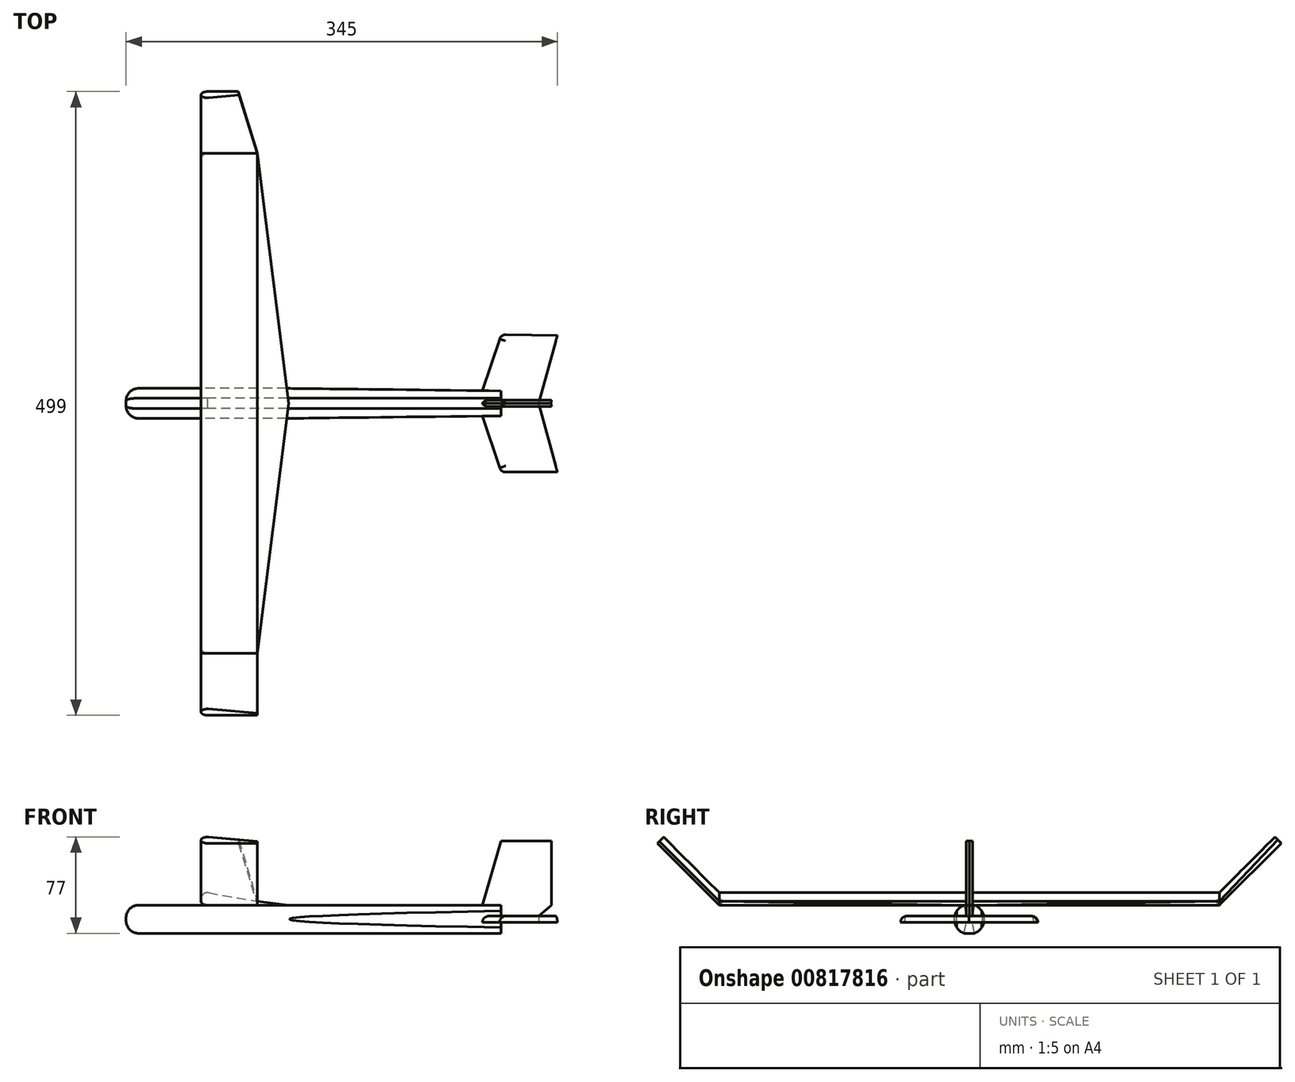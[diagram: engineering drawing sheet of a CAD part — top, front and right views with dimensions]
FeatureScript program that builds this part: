
annotation { "Feature Type Name" : "Feature", "Feature Type Description" : "" }
export const myFeature = defineFeature(function(context is Context, id is Id, definition is map)
    precondition{}
    {
        {
            var Q0;
            Q0=qCreatedBy(makeId("Top.planeOp"),FACE);
            var sketch = newSketch(context, id + "F0", { "sketchPlane" : qUnion([Q0])});
            skLineSegment(sketch, "E0", {"start": v(0, 0) * mm, "end": v(0, 200) * mm});
            skLineSegment(sketch, "E1", {"start": v(0, 0) * mm, "end": v(0, -200) * mm});
            skLineSegment(sketch, "E2", {"start": v(0, -200) * mm, "end": v(45, -200) * mm});
            skLineSegment(sketch, "E3", {"start": v(0, 200) * mm, "end": v(45, 200) * mm});
            skLineSegment(sketch, "E4", {"start": v(0, 0) * mm, "end": v(70, 0) * mm, "construction": true});
            skLineSegment(sketch, "E5", {"start": v(45, 200) * mm, "end": v(70, 0) * mm});
            skLineSegment(sketch, "E6", {"start": v(45, -200) * mm, "end": v(70, 0) * mm});
            skSolve(sketch);
        }
        {
            var Q0;
            Q0=makeQuery(id+"F0.imprint","IMPRINT",FACE,{"disambiguationData":[TD([[makeQuery(id+"F0.imprint","IMPRINT",EDGE,{"derivedFrom":sQuery(id+"F0.wireOp",EDGE,"E0")}),-1.0]])]});
            extrude(context, id + "F1", {"entities" : qUnion([Q0]), "depth" : 10 * mm, "offsetDistance" : 25 * mm});
        }
        {
            var Q0;
            Q0=makeQuery(id+"F1.opExtrude","SWEPT_FACE",FACE,{"disambiguationData":[OSD([sQuery(id+"F0.wireOp",EDGE,"E2")])]});
            var sketch = newSketch(context, id + "F2", { "sketchPlane" : qUnion([Q0])});
            skLineSegment(sketch, "E7.0.0", {"start": v(0, 0) * mm, "end": v(45, 0) * mm});
            skLineSegment(sketch, "E7.0.1", {"start": v(45, 0) * mm, "end": v(45, 10) * mm});
            skLineSegment(sketch, "E7.0.2", {"start": v(45, 10) * mm, "end": v(0, 10) * mm});
            skLineSegment(sketch, "E7.0.3", {"start": v(0, 10) * mm, "end": v(0, 5) * mm});
            skLineSegment(sketch, "E8.0.0", {"start": v(45, 0) * mm, "end": v(70, 0) * mm});
            skLineSegment(sketch, "E8.0.1", {"start": v(70, 0) * mm, "end": v(70, 10) * mm});
            skLineSegment(sketch, "E8.0.2", {"start": v(70, 10) * mm, "end": v(45, 10) * mm});
            skLineSegment(sketch, "E8.0.3", {"start": v(45, 10) * mm, "end": v(45, 0) * mm});
            skArc(sketch, "E9", {"start": v(5.87, 9.92) * mm, "mid": v(0.02, 5.44) * mm, "end": v(5, 0) * mm});
            skPoint(sketch, "E9.centerSnap0", {"position": v(0, 5) * mm});
            skLineSegment(sketch, "E10", {"start": v(5.87, 9.92) * mm, "end": v(45, 3) * mm});
            skLineSegment(sketch, "E11", {"start": v(45, 3) * mm, "end": v(70, 0) * mm});
            skSolve(sketch);
        }
        {
            var Q0;
            {var subQ5=sQuery(id+"F2.wireOp",EDGE,"E10");Q0=makeQuery(id+"F2.imprint","IMPRINT",FACE,{"disambiguationData":[TD([[makeQuery(id+"F2.imprint","IMPRINT",EDGE,{"derivedFrom":subQ5}),1.0]])]});}
            var Q1;
            Q1=makeQuery(id+"F2.imprint","IMPRINT",FACE,{"disambiguationData":[TD([[makeQuery(id+"F2.imprint","IMPRINT",EDGE,{"derivedFrom":sQuery(id+"F2.wireOp",EDGE,"E8.0.1")}),1.0]])]});
            var Q2;
            {var subQ0=sQuery(id+"F2.wireOp",EDGE,"E7.0.3");Q2=makeQuery(id+"F2.imprint","IMPRINT",FACE,{"disambiguationData":[TD([[makeQuery(id+"F2.imprint","IMPRINT",EDGE,{"derivedFrom":subQ0}),1.0]])]});}
            var Q3;
            {var subQ0=sQuery(id+"F2.wireOp",EDGE,"E7.0.0");var subQ3=sQuery(id+"F2.wireOp",EDGE,"E9");var subQ4=makeQuery(id+"F2.imprint","INTERSECT",VERTEX,{"derivedFrom":[subQ0,subQ3]});Q3=makeQuery(id+"F2.imprint","IMPRINT",FACE,{"disambiguationData":[TD([[makeQuery(id+"F2.imprint","IMPRINT",EDGE,{"disambiguationData":[TD([[subQ4,1.0]])],"derivedFrom":subQ0}),1.0]])]});}
            extrude(context, id + "F3", {"entities" : qUnion([Q0, Q1, Q2, Q3]), "operationType" : NewBodyOperationType.REMOVE, "oppositeDirection" : true, "depth" : 400 * mm, "offsetDistance" : 25 * mm});
        }
        {
            var Q0;
            Q0=qCreatedBy(makeId("Top.planeOp"),FACE);
            var sketch = newSketch(context, id + "F4", { "sketchPlane" : qUnion([Q0])});
            skLineSegment(sketch, "E12", {"start": v(0, 12) * mm, "end": v(0, -12) * mm});
            skLineSegment(sketch, "E13", {"start": v(0, -12) * mm, "end": v(-60, -12) * mm});
            skLineSegment(sketch, "E14", {"start": v(-60, -12) * mm, "end": v(-60, 12) * mm});
            skLineSegment(sketch, "E15", {"start": v(-60, 12) * mm, "end": v(0, 12) * mm});
            skLineSegment(sketch, "E16", {"start": v(0, -12) * mm, "end": v(70, -12) * mm});
            skLineSegment(sketch, "E17", {"start": v(70, -12) * mm, "end": v(70, 12) * mm});
            skLineSegment(sketch, "E18", {"start": v(70, 12) * mm, "end": v(0, 12) * mm});
            skLineSegment(sketch, "E19", {"start": v(0, 0) * mm, "end": v(240, 0) * mm, "construction": true});
            skPoint(sketch, "E19.endSnap0", {"position": v(70, 0) * mm});
            skLineSegment(sketch, "E20", {"start": v(240, -10) * mm, "end": v(240, 10) * mm});
            skLineSegment(sketch, "E21", {"start": v(240, -10) * mm, "end": v(70, -12) * mm});
            skLineSegment(sketch, "E22", {"start": v(70, 12) * mm, "end": v(240, 10) * mm});
            skSolve(sketch);
        }
        {
            var Q0;
            Q0=makeQuery(id+"F4.imprint","IMPRINT",FACE,{"disambiguationData":[TD([[makeQuery(id+"F4.imprint","IMPRINT",EDGE,{"derivedFrom":sQuery(id+"F4.wireOp",EDGE,"E12")}),1.0]])]});
            var Q1;
            Q1=makeQuery(id+"F4.imprint","IMPRINT",FACE,{"disambiguationData":[TD([[makeQuery(id+"F4.imprint","IMPRINT",EDGE,{"derivedFrom":sQuery(id+"F4.wireOp",EDGE,"E12")}),-1.0]])]});
            var Q2;
            Q2=makeQuery(id+"F4.imprint","IMPRINT",FACE,{"disambiguationData":[TD([[makeQuery(id+"F4.imprint","IMPRINT",EDGE,{"derivedFrom":sQuery(id+"F4.wireOp",EDGE,"E17")}),-1.0]])]});
            extrude(context, id + "F5", {"entities" : qUnion([Q0, Q1, Q2]), "operationType" : NewBodyOperationType.ADD, "oppositeDirection" : true, "depth" : 22.5 * mm, "offsetDistance" : 25 * mm});
        }
        {
            var Q0;
            Q0=makeQuery(id+"F5.opExtrude","SWEPT_FACE",FACE,{"disambiguationData":[OSD([sQuery(id+"F4.wireOp",EDGE,"E14")])]});
            var sketch = newSketch(context, id + "F6", { "sketchPlane" : qUnion([Q0])});
            skLineSegment(sketch, "E23.0.0", {"start": v(12, 0) * mm, "end": v(-12, 0) * mm});
            skLineSegment(sketch, "E23.0.1", {"start": v(-12, 0) * mm, "end": v(-12, -22.5) * mm});
            skLineSegment(sketch, "E23.0.2", {"start": v(-12, -22.5) * mm, "end": v(12, -22.5) * mm});
            skLineSegment(sketch, "E23.0.3", {"start": v(12, -22.5) * mm, "end": v(12, 0) * mm});
            skCircle(sketch, "E24", {"center": v(0, -11.25) * mm, "radius": 12 * mm});
            skPoint(sketch, "E24.centerSnap0", {"position": v(-12, -11.25) * mm});
            skSolve(sketch);
        }
        {
            var Q0;
            {var subQ0=sQuery(id+"F6.wireOp",EDGE,"E23.0.1");var subQ1=sQuery(id+"F6.wireOp",EDGE,"E23.0.0");var subQ2=makeQuery(id+"F6.imprint","INTERSECT",VERTEX,{"derivedFrom":[subQ1,subQ0]});Q0=makeQuery(id+"F6.imprint","IMPRINT",FACE,{"disambiguationData":[TD([[makeQuery(id+"F6.imprint","IMPRINT",EDGE,{"disambiguationData":[TD([[subQ2,1.0]])],"derivedFrom":subQ1}),1.0]])]});}
            var Q1;
            {var subQ0=sQuery(id+"F6.wireOp",EDGE,"E23.0.3");var subQ1=sQuery(id+"F6.wireOp",EDGE,"E23.0.0");var subQ2=makeQuery(id+"F6.imprint","INTERSECT",VERTEX,{"derivedFrom":[subQ1,subQ0]});Q1=makeQuery(id+"F6.imprint","IMPRINT",FACE,{"disambiguationData":[TD([[makeQuery(id+"F6.imprint","IMPRINT",EDGE,{"disambiguationData":[TD([[subQ2,-1.0]])],"derivedFrom":subQ1}),1.0]])]});}
            var Q2;
            {var subQ0=sQuery(id+"F6.wireOp",EDGE,"E23.0.3");var subQ1=sQuery(id+"F6.wireOp",EDGE,"E23.0.2");var subQ2=makeQuery(id+"F6.imprint","INTERSECT",VERTEX,{"derivedFrom":[subQ1,subQ0]});Q2=makeQuery(id+"F6.imprint","IMPRINT",FACE,{"disambiguationData":[TD([[makeQuery(id+"F6.imprint","IMPRINT",EDGE,{"disambiguationData":[TD([[subQ2,-1.0]])],"derivedFrom":subQ1}),-1.0]])]});}
            var Q3;
            {var subQ0=sQuery(id+"F6.wireOp",EDGE,"E23.0.2");var subQ1=sQuery(id+"F6.wireOp",EDGE,"E23.0.1");var subQ2=makeQuery(id+"F6.imprint","INTERSECT",VERTEX,{"derivedFrom":[subQ1,subQ0]});Q3=makeQuery(id+"F6.imprint","IMPRINT",FACE,{"disambiguationData":[TD([[makeQuery(id+"F6.imprint","IMPRINT",EDGE,{"disambiguationData":[TD([[subQ2,-1.0]])],"derivedFrom":subQ1}),-1.0]])]});}
            extrude(context, id + "F7", {"entities" : qUnion([Q0, Q1, Q2, Q3]), "operationType" : NewBodyOperationType.REMOVE, "oppositeDirection" : true, "depth" : 300 * mm, "offsetDistance" : 25 * mm});
        }
        {
            var Q0;
            Q0=makeQuery(id+"F5.opExtrude","SWEPT_FACE",FACE,{"disambiguationData":[OSD([sQuery(id+"F4.wireOp",EDGE,"E14")])]});
            fillet(context, id + "F8", {"entities" : qUnion([Q0]), "radius" : 10 * mm, "tangentPropagation" : true, "allowEdgeOverflow" : false});
        }
        {
            var Q0;
            {var subQ0=sQuery(id+"F0.wireOp",EDGE,"E5");var subQ2=sQuery(id+"F4.wireOp",EDGE,"E21");var subQ3=sQuery(id+"F4.wireOp",EDGE,"E16");var subQ4=sQuery(id+"F4.wireOp",EDGE,"E13");var subQ5=sQuery(id+"F4.wireOp",EDGE,"E18");var subQ6=sQuery(id+"F4.wireOp",EDGE,"E15");var subQ7=sQuery(id+"F4.wireOp",EDGE,"E20");var subQ8=sQuery(id+"F4.wireOp",EDGE,"E22");Q0=makeQuery(id+"F5.boolean.opBoolean","SPLIT",FACE,{"disambiguationData":[TD([makeQuery(id+"F1.opExtrude","SWEPT_FACE",FACE,{"disambiguationData":[OSD([subQ0])]})])],"derivedFrom":makeQuery(id+"F5.opExtrude","CAP_FACE",FACE,{"disambiguationData":[OSD([subQ4,sQuery(id+"F4.wireOp",EDGE,"E14"),subQ6,subQ3,subQ5,subQ7,subQ2,subQ8])],"isStart":true})});}
            cPlane(context, id + "F9", {"entities" : qUnion([Q0]), "cplaneType" : CPlaneType.OFFSET, "offset" : 11.25 * mm, "oppositeDirection" : true, "width" : 150 * mm, "height" : 150 * mm});
        }
        {
            var Q0;
            Q0=qCreatedBy(id+"F9.planeOp",FACE);
            var sketch = newSketch(context, id + "F10", { "sketchPlane" : qUnion([Q0])});
            skLineSegment(sketch, "E25.0", {"start": v(240, 10) * mm, "end": v(70, 12) * mm});
            skLineSegment(sketch, "E26.0", {"start": v(240, -4.18) * mm, "end": v(240, 4.18) * mm});
            skLineSegment(sketch, "E27.0", {"start": v(240, 4.18) * mm, "end": v(240, 10) * mm});
            skLineSegment(sketch, "E28.0", {"start": v(240, -10) * mm, "end": v(240, -4.18) * mm});
            skLineSegment(sketch, "E29.0", {"start": v(240, -10) * mm, "end": v(70, -12) * mm});
            skLineSegment(sketch, "E30", {"start": v(240, 0) * mm, "end": v(225, 0.18) * mm, "construction": true});
            skLineSegment(sketch, "E31", {"start": v(240, 0) * mm, "end": v(270, -0.35) * mm, "construction": true});
            skPoint(sketch, "E32", {"position": v(230, 0.12) * mm});
            skLineSegment(sketch, "E33", {"start": v(230, 0.12) * mm, "end": v(230, 10.12) * mm, "construction": true});
            skLineSegment(sketch, "E34", {"start": v(230, 0.12) * mm, "end": v(230, -10.12) * mm, "construction": true});
            skLineSegment(sketch, "E35", {"start": v(225, -10.18) * mm, "end": v(225, 10.18) * mm, "construction": true});
            skLineSegment(sketch, "E36", {"start": v(240, 0) * mm, "end": v(240, 55) * mm, "construction": true});
            skLineSegment(sketch, "E37", {"start": v(240, 0) * mm, "end": v(240, -55) * mm, "construction": true});
            skLineSegment(sketch, "E38", {"start": v(240, -55) * mm, "end": v(285, -55) * mm});
            skLineSegment(sketch, "E39", {"start": v(285, -55) * mm, "end": v(270, -0.35) * mm});
            skLineSegment(sketch, "E40", {"start": v(240, 55) * mm, "end": v(285, 54.47) * mm});
            skLineSegment(sketch, "E41", {"start": v(285, 54.47) * mm, "end": v(270, -0.35) * mm});
            skLineSegment(sketch, "E42", {"start": v(240, 55) * mm, "end": v(225, 10.18) * mm});
            skLineSegment(sketch, "E43", {"start": v(240, -55) * mm, "end": v(225, -10.18) * mm});
            skSolve(sketch);
        }
        {
            var Q0;
            Q0=makeQuery(id+"F10.imprint","IMPRINT",FACE,{"disambiguationData":[TD([[makeQuery(id+"F10.imprint","IMPRINT",EDGE,{"derivedFrom":sQuery(id+"F10.wireOp",EDGE,"E26.0")}),-1.0]])]});
            extrude(context, id + "F11", {"entities" : qUnion([Q0]), "operationType" : NewBodyOperationType.ADD, "endBound" : BoundingType.SYMMETRIC, "depth" : 5 * mm, "offsetDistance" : 25 * mm});
        }
        {
            var Q0;
            Q0=qCreatedBy(makeId("Front.planeOp"),FACE);
            var sketch = newSketch(context, id + "F12", { "sketchPlane" : qUnion([Q0])});
            skLineSegment(sketch, "E44.0", {"start": v(240, -8.75) * mm, "end": v(285, -8.75) * mm});
            skLineSegment(sketch, "E45.0", {"start": v(240, -8.75) * mm, "end": v(240, -4.62) * mm});
            skLineSegment(sketch, "E46.0", {"start": v(240, -4.62) * mm, "end": v(240, 0) * mm});
            skLineSegment(sketch, "E47.0", {"start": v(240, 0) * mm, "end": v(69.48, 0) * mm});
            skLineSegment(sketch, "E48.0", {"start": v(240, -8.75) * mm, "end": v(225, -8.75) * mm});
            skLineSegment(sketch, "E49", {"start": v(225, -8.75) * mm, "end": v(225, 0) * mm, "construction": true});
            skLineSegment(sketch, "E50", {"start": v(240, -8.75) * mm, "end": v(240, 51.25) * mm, "construction": true});
            skPoint(sketch, "E51", {"position": v(270, -8.75) * mm});
            skLineSegment(sketch, "E52", {"start": v(225, 0) * mm, "end": v(240, 51.25) * mm});
            skLineSegment(sketch, "E53", {"start": v(280, 51.25) * mm, "end": v(240, 51.25) * mm});
            skLineSegment(sketch, "E54", {"start": v(280, 0) * mm, "end": v(270, -8.75) * mm});
            skLineSegment(sketch, "E55", {"start": v(280, 51.25) * mm, "end": v(280, 0) * mm});
            skSolve(sketch);
        }
        {
            var Q0;
            {var subQ3=sQuery(id+"F12.wireOp",EDGE,"E45.0");Q0=makeQuery(id+"F12.imprint","IMPRINT",FACE,{"disambiguationData":[TD([[makeQuery(id+"F12.imprint","IMPRINT",EDGE,{"derivedFrom":subQ3}),-1.0]])]});}
            extrude(context, id + "F13", {"entities" : qUnion([Q0]), "operationType" : NewBodyOperationType.ADD, "endBound" : BoundingType.SYMMETRIC, "depth" : 5 * mm, "offsetDistance" : 25 * mm, "hasDraft" : true, "draftAngle" : 3 * degree});
        }
        {
            var Q0;
            Q0=makeQuery(id+"F11.opExtrude","CAP_EDGE",EDGE,{"disambiguationData":[OSD([sQuery(id+"F10.wireOp",EDGE,"E42")])],"isStart":false});
            var Q1;
            Q1=makeQuery(id+"F11.opExtrude","CAP_EDGE",EDGE,{"disambiguationData":[OSD([sQuery(id+"F10.wireOp",EDGE,"E43")])],"isStart":false});
            fillet(context, id + "F14", {"entities" : qUnion([Q0, Q1]), "radius" : 5 * mm, "tangentPropagation" : true, "allowEdgeOverflow" : false});
        }
        {
            var Q0;
            Q0=makeQuery(id+"F13.opExtrude","CAP_EDGE",EDGE,{"disambiguationData":[OSD([sQuery(id+"F12.wireOp",EDGE,"E52")])],"isStart":true});
            var Q1;
            Q1=makeQuery(id+"F13.opExtrude","CAP_EDGE",EDGE,{"disambiguationData":[OSD([sQuery(id+"F12.wireOp",EDGE,"E52")])],"isStart":false});
            fillet(context, id + "F15", {"entities" : qUnion([Q0, Q1]), "radius" : 5 * mm, "tangentPropagation" : true, "allowEdgeOverflow" : false});
        }
        {
            var Q0;
            Q0=qCreatedBy(makeId("Right.planeOp"),FACE);
            var sketch = newSketch(context, id + "F16", { "sketchPlane" : qUnion([Q0])});
            skLineSegment(sketch, "E56.0", {"start": v(-200, 0) * mm, "end": v(-200, 10) * mm});
            skLineSegment(sketch, "E57.0", {"start": v(-4.18, 0) * mm, "end": v(-200, 0) * mm});
            skLineSegment(sketch, "E58", {"start": v(-200, 0) * mm, "end": v(-192.93, -7.07) * mm});
            skLineSegment(sketch, "E59.MirrorCS", {"start": v(-200, 0) * mm, "end": v(-207.07, -7.07) * mm});
            skLineSegment(sketch, "E60.0", {"start": v(200, 0) * mm, "end": v(4.18, 0) * mm});
            skLineSegment(sketch, "E61.0", {"start": v(200, 0) * mm, "end": v(200, 10) * mm});
            skLineSegment(sketch, "E62", {"start": v(200, 0) * mm, "end": v(192.93, -7.07) * mm});
            skSolve(sketch);
        }
        {
            var Q0;
            Q0=sQuery(id+"F16.wireOp",VERTEX,"E56.0.start");
            var Q1;
            Q1=sQuery(id+"F16.wireOp",EDGE,"E58");
            cPlane(context, id + "F17", {"entities" : qUnion([Q0, Q1]), "cplaneType" : CPlaneType.LINE_POINT, "offset" : 25 * mm, "width" : 150 * mm, "height" : 150 * mm});
        }
        {
            var Q0;
            Q0=qCreatedBy(id+"F17.planeOp",FACE);
            var sketch = newSketch(context, id + "F18", { "sketchPlane" : qUnion([Q0])});
            skLineSegment(sketch, "E63.0.0", {"start": v(-45, -139.3) * mm, "end": v(-5.87, -134.4) * mm});
            skEllipticalArc(sketch, "E63.0.1", {});
            skLineSegment(sketch, "E63.0.2", {"start": v(-5, -141.42) * mm, "end": v(-45, -141.42) * mm});
            skLineSegment(sketch, "E63.0.3", {"start": v(-45, -141.42) * mm, "end": v(-45, -139.3) * mm});
            const initialGuessF18  = {"E63.0.1": [-0.005, -0.13788582233137678, -1, 0, 0.005, 0.003535533905932738, 1.5707963267948966, 4.887518018304354]};
            skSetInitialGuess(sketch, initialGuessF18);
            skSolve(sketch);
        }
        {
            var Q0;
            Q0=makeQuery(id+"F18.imprint","IMPRINT",FACE,{"disambiguationData":[TD([[makeQuery(id+"F18.imprint","IMPRINT",EDGE,{"derivedFrom":sQuery(id+"F18.wireOp",EDGE,"E63.0.0")}),-1.0]])]});
            extrude(context, id + "F19", {"entities" : qUnion([Q0]), "operationType" : NewBodyOperationType.ADD, "oppositeDirection" : true, "depth" : 70 * mm, "offsetDistance" : 25 * mm});
        }
        {
            var Q0;
            Q0=sQuery(id+"F16.wireOp",VERTEX,"E60.0.start");
            var Q1;
            Q1=sQuery(id+"F16.wireOp",EDGE,"E62");
            cPlane(context, id + "F20", {"entities" : qUnion([Q0, Q1]), "cplaneType" : CPlaneType.LINE_POINT, "offset" : 25 * mm, "width" : 150 * mm, "height" : 150 * mm});
        }
        {
            var Q0;
            Q0=qCreatedBy(id+"F20.planeOp",FACE);
            var sketch = newSketch(context, id + "F21", { "sketchPlane" : qUnion([Q0])});
            skEllipticalArc(sketch, "E64.0.0", {});
            skLineSegment(sketch, "E64.0.1", {"start": v(5.87, -134.4) * mm, "end": v(45, -139.3) * mm});
            skLineSegment(sketch, "E64.0.2", {"start": v(45, -139.3) * mm, "end": v(45, -141.42) * mm});
            skLineSegment(sketch, "E64.0.3", {"start": v(45, -141.42) * mm, "end": v(5, -141.42) * mm});
            const initialGuessF21  = {"E64.0.0": [0.005, -0.13788582233137678, -1, 0, 0.005, 0.0035355339059327372, 4.537259942465023, 1.5707963267948966]};
            skSetInitialGuess(sketch, initialGuessF21);
            skSolve(sketch);
        }
        {
            var Q0;
            Q0=makeQuery(id+"F21.imprint","IMPRINT",FACE,{"disambiguationData":[TD([[makeQuery(id+"F21.imprint","IMPRINT",EDGE,{"derivedFrom":sQuery(id+"F21.wireOp",EDGE,"E64.0.0")}),1.0]])]});
            extrude(context, id + "F22", {"entities" : qUnion([Q0]), "operationType" : NewBodyOperationType.ADD, "oppositeDirection" : true, "depth" : 70 * mm, "offsetDistance" : 25 * mm});
        }
        {
            var Q0;
            Q0=makeQuery(id+"F19.opExtrude","SWEPT_FACE",FACE,{"disambiguationData":[OSD([sQuery(id+"F18.wireOp",EDGE,"E63.0.0")])]});
            var sketch = newSketch(context, id + "F23", { "sketchPlane" : qUnion([Q0])});
            skLineSegment(sketch, "E65.0", {"start": v(61.95, -211.42) * mm, "end": v(22.51, -211.42) * mm});
            skLineSegment(sketch, "E66.0", {"start": v(61.95, -211.42) * mm, "end": v(61.95, -143.54) * mm});
            skLineSegment(sketch, "E67.0", {"start": v(22.52, -211.42) * mm, "end": v(17.1, -211.42) * mm});
            skPoint(sketch, "E68", {"position": v(47.1, -211.42) * mm});
            skLineSegment(sketch, "E69", {"start": v(61.95, -143.54) * mm, "end": v(47.1, -211.42) * mm});
            skLineSegment(sketch, "E70.0", {"start": v(62.2, -211.42) * mm, "end": v(62.2, -141.42) * mm});
            skLineSegment(sketch, "E71", {"start": v(61.95, -143.54) * mm, "end": v(62.2, -141.42) * mm});
            skLineSegment(sketch, "E72", {"start": v(61.95, -211.42) * mm, "end": v(62.2, -211.42) * mm});
            skSolve(sketch);
        }
        {
            var Q0;
            {var subQ0=sQuery(id+"F23.wireOp",EDGE,"E66.0");Q0=makeQuery(id+"F23.imprint","IMPRINT",FACE,{"disambiguationData":[TD([[makeQuery(id+"F23.imprint","IMPRINT",EDGE,{"derivedFrom":subQ0}),1.0]])]});}
            var Q1;
            Q1=makeQuery(id+"F23.imprint","IMPRINT",FACE,{"disambiguationData":[TD([[makeQuery(id+"F23.imprint","IMPRINT",EDGE,{"derivedFrom":sQuery(id+"F23.wireOp",EDGE,"E66.0")}),-1.0]])]});
            extrude(context, id + "F24", {"entities" : qUnion([Q0, Q1]), "operationType" : NewBodyOperationType.REMOVE, "oppositeDirection" : true, "depth" : 5 * mm, "offsetDistance" : 25 * mm});
        }
        {
            var Q0;
            Q0=makeQuery(id+"F22.opExtrude","SWEPT_FACE",FACE,{"disambiguationData":[OSD([sQuery(id+"F21.wireOp",EDGE,"E64.0.1")])]});
            var sketch = newSketch(context, id + "F25", { "sketchPlane" : qUnion([Q0])});
            skLineSegment(sketch, "E73.0", {"start": v(61.95, 211.42) * mm, "end": v(61.95, 143.54) * mm});
            skLineSegment(sketch, "E74.0", {"start": v(22.51, 211.42) * mm, "end": v(61.95, 211.42) * mm});
            skLineSegment(sketch, "E75.0", {"start": v(62.2, 211.42) * mm, "end": v(62.2, 141.42) * mm});
            skLineSegment(sketch, "E76", {"start": v(62.2, 211.42) * mm, "end": v(61.95, 211.42) * mm});
            skLineSegment(sketch, "E77", {"start": v(61.95, 143.54) * mm, "end": v(62.2, 141.42) * mm});
            skLineSegment(sketch, "E78.0", {"start": v(17.1, 211.42) * mm, "end": v(22.52, 211.42) * mm});
            skPoint(sketch, "E79", {"position": v(47.1, 211.42) * mm});
            skLineSegment(sketch, "E80", {"start": v(47.1, 211.42) * mm, "end": v(61.95, 143.54) * mm});
            skSolve(sketch);
        }
        {
            var Q0;
            {var subQ0=sQuery(id+"F25.wireOp",EDGE,"E73.0");Q0=makeQuery(id+"F25.imprint","IMPRINT",FACE,{"disambiguationData":[TD([[makeQuery(id+"F25.imprint","IMPRINT",EDGE,{"derivedFrom":subQ0}),-1.0]])]});}
            var Q1;
            Q1=makeQuery(id+"F25.imprint","IMPRINT",FACE,{"disambiguationData":[TD([[makeQuery(id+"F25.imprint","IMPRINT",EDGE,{"derivedFrom":sQuery(id+"F25.wireOp",EDGE,"E73.0")}),1.0]])]});
            extrude(context, id + "F26", {"entities" : qUnion([Q0, Q1]), "operationType" : NewBodyOperationType.REMOVE, "oppositeDirection" : true, "depth" : 5 * mm, "offsetDistance" : 25 * mm});
        }
        {
            var Q0;
            Q0=makeQuery(id+"F11.opExtrude","CAP_EDGE",EDGE,{"disambiguationData":[OSD([sQuery(id+"F10.wireOp",EDGE,"E38")])],"isStart":false});
            var Q1;
            Q1=makeQuery(id+"F11.opExtrude","CAP_EDGE",EDGE,{"disambiguationData":[OSD([sQuery(id+"F10.wireOp",EDGE,"E40")])],"isStart":false});
            fillet(context, id + "F27", {"entities" : qUnion([Q0, Q1]), "radius" : 5 * mm, "tangentPropagation" : true, "allowEdgeOverflow" : false});
        }
    });
